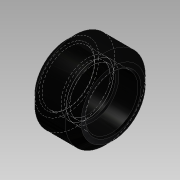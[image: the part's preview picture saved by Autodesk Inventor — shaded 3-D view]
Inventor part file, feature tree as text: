
AUTODESK INVENTOR PART (.ipt)
format: ipt  version: 2015 (Build 190159000, 159)  size: 123,392 bytes
history: native  units: mm
features: revolve x1, sketch x1
ambient origin geometry x8: Origin, YZ Plane, XZ Plane, XY Plane, X Axis, Y Axis, Z Axis, Center Point
bodies: Solid1 (feature_tree)
feature tree (2):
  revolve  "Revolution1"  [1 undecoded]
  sketch  "Sketch1"  dims[d0=5.0mm d1=20.0mm d2=90.0deg d3=8.64mm d4=15.23mm d5=0.5mm d6=3.9mm d7=12.21mm d8=9.974mm d9=135.0deg d10=0.3mm d11=0.3mm d12=5.78mm d13=90.0deg]
note: 1 required parameter value undecoded (feature->parameter linkage not recoverable at this tier; creation-order binding heuristic only, values carry confidence <= 0.55)
